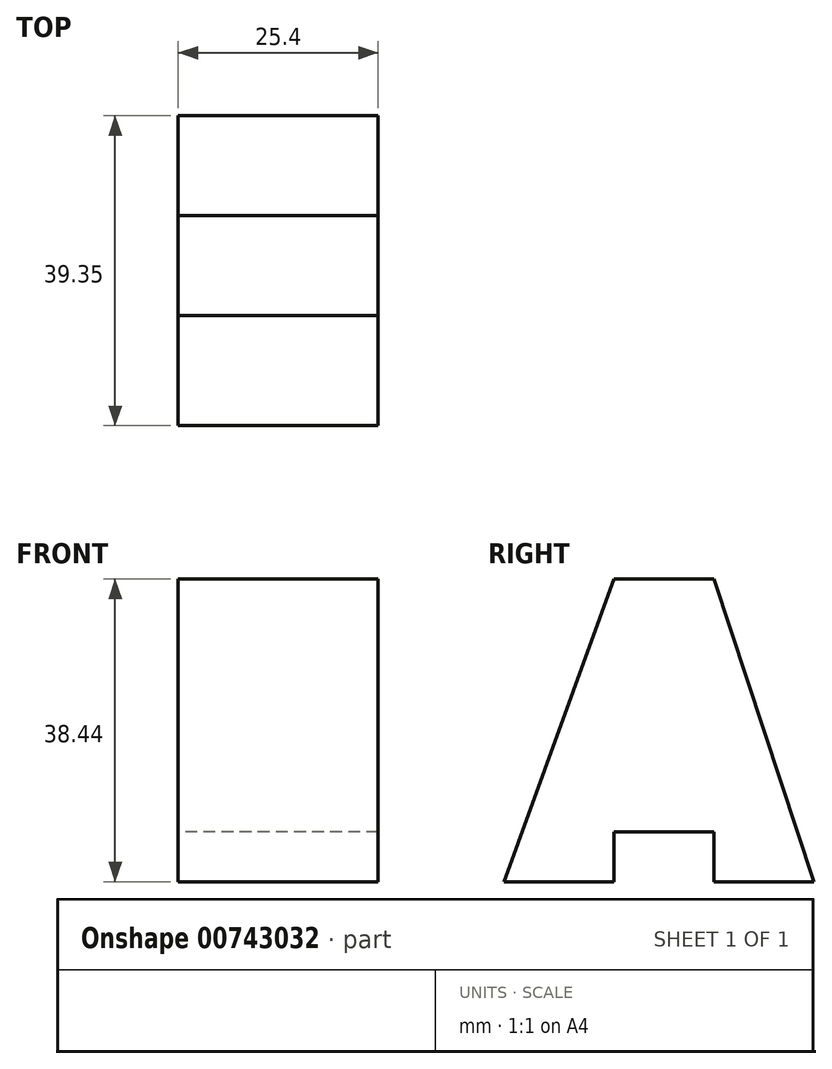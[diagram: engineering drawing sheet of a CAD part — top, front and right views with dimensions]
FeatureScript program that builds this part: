
annotation { "Feature Type Name" : "Feature", "Feature Type Description" : "" }
export const myFeature = defineFeature(function(context is Context, id is Id, definition is map)
    precondition{}
    {
        {
            var Q0;
            Q0=qCreatedBy(makeId("Right.planeOp"),FACE);
            var sketch = newSketch(context, id + "F0", { "sketchPlane" : qUnion([Q0])});
            skLineSegment(sketch, "E0", {"start": v(0, 0) * mm, "end": v(-12.7, 38.44) * mm});
            skLineSegment(sketch, "E1", {"start": v(-12.7, 38.44) * mm, "end": v(-25.4, 38.44) * mm});
            skLineSegment(sketch, "E2", {"start": v(-25.4, 38.44) * mm, "end": v(-39.35, 0) * mm});
            skLineSegment(sketch, "E3", {"start": v(-39.35, 0) * mm, "end": v(-25.4, 0) * mm});
            skLineSegment(sketch, "E4", {"start": v(-25.4, 0) * mm, "end": v(-25.4, 6.35) * mm});
            skLineSegment(sketch, "E5", {"start": v(-25.4, 6.35) * mm, "end": v(-12.7, 6.35) * mm});
            skLineSegment(sketch, "E6", {"start": v(-12.7, 6.35) * mm, "end": v(-12.7, 0) * mm});
            skLineSegment(sketch, "E7", {"start": v(-12.7, 0) * mm, "end": v(0, 0) * mm});
            skSolve(sketch);
        }
        {
            var Q0;
            Q0 = qSketchRegion(id + "F0", true);
            extrude(context, id + "F1", {"entities" : qUnion([Q0]), "depth" : 25.4 * mm, "offsetDistance" : 25.4 * mm});
        }
    });
